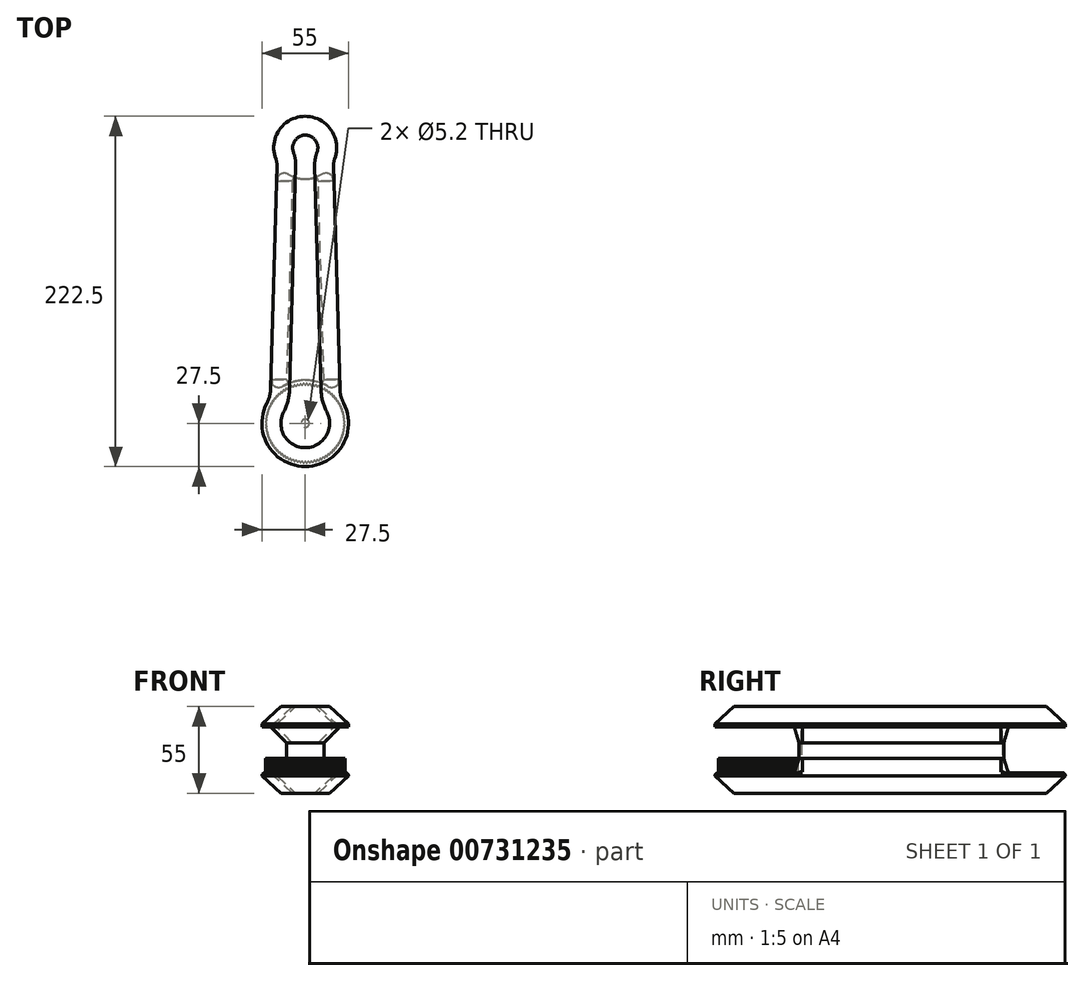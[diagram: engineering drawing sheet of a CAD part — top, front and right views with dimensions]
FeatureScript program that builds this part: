
annotation { "Feature Type Name" : "Feature", "Feature Type Description" : "" }
export const myFeature = defineFeature(function(context is Context, id is Id, definition is map)
    precondition{}
    {
        {
            assignVariable(context, id + "F0", {"name" : "Teeth", "anyValue" : 80});
        }
        {
            var Q0;
            Q0=qCreatedBy(makeId("Top.planeOp"),FACE);
            var sketch = newSketch(context, id + "F1", { "sketchPlane" : qUnion([Q0])});
            skCircle(sketch, "E0", {"center": v(0, 0) * mm, "radius": 25.21 * mm});
            skSolve(sketch);
        }
        {
            var Q0;
            Q0=qCreatedBy(makeId("Top.planeOp"),FACE);
            var sketch = newSketch(context, id + "F2", { "sketchPlane" : qUnion([Q0])});
            skArc(sketch, "E1.0", {"start": v(0.79, 25.2) * mm, "mid": v(0, 25.21) * mm, "end": v(-0.79, 25.2) * mm});
            skLineSegment(sketch, "E2", {"start": v(0, 0) * mm, "end": v(0, 25.03) * mm, "construction": true});
            skArc(sketch, "E3", {"start": v(0, 24.42) * mm, "mid": v(-0.38, 24.56) * mm, "end": v(-0.6, 24.9) * mm});
            skArc(sketch, "E4", {"start": v(-0.6, 24.9) * mm, "mid": v(-0.63, 25) * mm, "end": v(-0.68, 25.1) * mm});
            skArc(sketch, "E5", {"start": v(-0.68, 25.1) * mm, "mid": v(-0.72, 25.16) * mm, "end": v(-0.79, 25.2) * mm});
            skArc(sketch, "E6.MirrorCS", {"start": v(0, 24.42) * mm, "mid": v(0.38, 24.56) * mm, "end": v(0.6, 24.9) * mm});
            skArc(sketch, "E7.MirrorCS", {"start": v(0.68, 25.1) * mm, "mid": v(0.72, 25.16) * mm, "end": v(0.79, 25.2) * mm});
            skArc(sketch, "E8.MirrorCS", {"start": v(0.6, 24.9) * mm, "mid": v(0.63, 25) * mm, "end": v(0.68, 25.1) * mm});
            skSolve(sketch);
        }
        {
            var Q0;
            Q0=qSketchRegion(id+"F1",true);
            extrude(context, id + "F3", {"entities" : qUnion([Q0]), "depth" : 9 * mm, "offsetDistance" : 25 * mm});
        }
        {
            var Q0;
            Q0=makeQuery(id+"F2.imprint","IMPRINT",FACE,{"disambiguationData":[TD([[makeQuery(id+"F2.imprint","IMPRINT",EDGE,{"derivedFrom":sQuery(id+"F2.wireOp",EDGE,"E1.0")}),1.0]])]});
            extrude(context, id + "F4", {"entities" : qUnion([Q0]), "depth" : 25 * mm, "offsetDistance" : 25 * mm});
        }
        {
            var Q0;
            Q0=makeQuery(id+"F4.opExtrude","SWEPT_BODY",BODY,{"disambiguationData":[OSD([sQuery(id+"F2.wireOp",EDGE,"E1.0"),sQuery(id+"F2.wireOp",EDGE,"E3"),sQuery(id+"F2.wireOp",EDGE,"E4"),sQuery(id+"F2.wireOp",EDGE,"E5"),sQuery(id+"F2.wireOp",EDGE,"E6.MirrorCS"),sQuery(id+"F2.wireOp",EDGE,"E7.MirrorCS"),sQuery(id+"F2.wireOp",EDGE,"E8.MirrorCS")])]});
            var Q1;
            Q1=sQuery(id+"F1.wireOp",EDGE,"E0");
            circularPattern(context, id + "F5", {"operationType" : NewBodyOperationType.REMOVE, "entities" : qUnion([Q0]), "axis" : qUnion([Q1]), "angle" : 360 * degree, "instanceCount" : getVariable(context, 'Teeth'), "equalSpace" : true});
        }
        {
            var Q0;
            Q0=qCreatedBy(makeId("Top.planeOp"),FACE);
            var sketch = newSketch(context, id + "F6", { "sketchPlane" : qUnion([Q0])});
            skCircle(sketch, "E9", {"center": v(0, 0) * mm, "radius": 2.6 * mm});
            skSolve(sketch);
        }
        {
            var Q0;
            Q0=qSketchRegion(id+"F6",true);
            var Q1;
            Q1=sQuery(id+"F6.wireOp",EDGE,"E9");
            extrude(context, id + "F7", {"entities" : qUnion([Q0]), "operationType" : NewBodyOperationType.REMOVE, "surfaceEntities" : qUnion([Q1]), "endBound" : BoundingType.THROUGH_ALL, "depth" : 25 * mm, "offsetDistance" : 25 * mm});
        }
        {
            var Q0;
            Q0=makeQuery(id+"F3.opExtrude","SWEPT_BODY",BODY,{"disambiguationData":[OSD([sQuery(id+"F1.wireOp",EDGE,"E0")])]});
            transform(context, id + "F8", {"entities" : qUnion([Q0]), "transformType" : TransformType.TRANSLATION_3D, "dx" : 0 * mm, "dy" : 0 * mm, "dz" : 0 * mm, "makeCopy" : true});
        }
        {
            var Q0;
            Q0=qCreatedBy(makeId("Top.planeOp"),FACE);
            var sketch = newSketch(context, id + "F9", { "sketchPlane" : qUnion([Q0])});
            skArc(sketch, "E10", {"start": v(-24.31, 12.85) * mm, "mid": v(0, -27.5) * mm, "end": v(24.31, 12.85) * mm});
            skLineSegment(sketch, "E11", {"start": v(0, 0) * mm, "end": v(0, 175) * mm, "construction": true});
            skArc(sketch, "E12", {"start": v(18.66, 167.81) * mm, "mid": v(0, 195) * mm, "end": v(-18.66, 167.81) * mm});
            skLineSegment(sketch, "E13", {"start": v(-18, 163.94) * mm, "end": v(-22, 21.64) * mm});
            skArc(sketch, "E14.filletArc", {"start": v(-24.31, 12.85) * mm, "mid": v(-22.65, 17.11) * mm, "end": v(-22, 21.64) * mm});
            skArc(sketch, "E15.filletArc", {"start": v(-18, 163.94) * mm, "mid": v(-18.14, 165.9) * mm, "end": v(-18.66, 167.81) * mm});
            skLineSegment(sketch, "E16.MirrorCS", {"start": v(18, 163.94) * mm, "end": v(22, 21.64) * mm});
            skArc(sketch, "E17.MirrorCS", {"start": v(18, 163.94) * mm, "mid": v(18.14, 165.9) * mm, "end": v(18.66, 167.81) * mm});
            skArc(sketch, "E18.MirrorCS", {"start": v(24.31, 12.85) * mm, "mid": v(22.65, 17.11) * mm, "end": v(22, 21.64) * mm});
            skSolve(sketch);
        }
        {
            var Q0;
            Q0=makeQuery(id+"F9.imprint","IMPRINT",FACE,{"disambiguationData":[TD([[makeQuery(id+"F9.imprint","IMPRINT",EDGE,{"derivedFrom":sQuery(id+"F9.wireOp",EDGE,"E10")}),1.0]])]});
            extrude(context, id + "F10", {"entities" : qUnion([Q0]), "oppositeDirection" : true, "depth" : 2 * mm, "offsetDistance" : 25 * mm});
        }
        {
            var Q0;
            Q0=makeQuery(id+"F10.opExtrude","CAP_FACE",FACE,{"disambiguationData":[OSD([sQuery(id+"F9.wireOp",EDGE,"E10"),sQuery(id+"F9.wireOp",EDGE,"E12"),sQuery(id+"F9.wireOp",EDGE,"E13"),sQuery(id+"F9.wireOp",EDGE,"E14.filletArc"),sQuery(id+"F9.wireOp",EDGE,"E15.filletArc"),sQuery(id+"F9.wireOp",EDGE,"E16.MirrorCS"),sQuery(id+"F9.wireOp",EDGE,"E17.MirrorCS"),sQuery(id+"F9.wireOp",EDGE,"E18.MirrorCS")])],"isStart":true});
            var sketch = newSketch(context, id + "F11", { "sketchPlane" : qUnion([Q0])});
            skArc(sketch, "E19", {"start": v(14.24, 23.53) * mm, "mid": v(0, 27.5) * mm, "end": v(-14.24, 23.53) * mm});
            skArc(sketch, "E20.0.0", {"start": v(18, 163.94) * mm, "mid": v(18.14, 165.9) * mm, "end": v(18.66, 167.81) * mm});
            skArc(sketch, "E20.0.1", {"start": v(18.66, 167.81) * mm, "mid": v(0, 195) * mm, "end": v(-18.66, 167.81) * mm});
            skArc(sketch, "E20.0.2", {"start": v(-18.66, 167.81) * mm, "mid": v(-18.14, 165.9) * mm, "end": v(-18, 163.94) * mm});
            skLineSegment(sketch, "E20.0.3", {"start": v(-18.28, 153.96) * mm, "end": v(-21.82, 27.95) * mm});
            skArc(sketch, "E20.0.5", {"start": v(-24.31, 12.85) * mm, "mid": v(0, -27.5) * mm, "end": v(24.31, 12.85) * mm});
            skLineSegment(sketch, "E20.0.7", {"start": v(21.82, 27.95) * mm, "end": v(18.28, 153.96) * mm});
            skPoint(sketch, "E21.newPointB", {"position": v(-22, 21.64) * mm});
            skArc(sketch, "E21.filletArc", {"start": v(-21.82, 27.95) * mm, "mid": v(-19.34, 23.49) * mm, "end": v(-14.24, 23.53) * mm});
            skPoint(sketch, "E22.newPointB", {"position": v(22, 21.64) * mm});
            skArc(sketch, "E22.filletArc", {"start": v(14.24, 23.53) * mm, "mid": v(19.34, 23.49) * mm, "end": v(21.82, 27.95) * mm});
            skArc(sketch, "E23", {"start": v(-10.63, 158.06) * mm, "mid": v(0, 155) * mm, "end": v(10.63, 158.06) * mm});
            skArc(sketch, "E24.filletArc", {"start": v(-10.63, 158.06) * mm, "mid": v(-15.64, 158.23) * mm, "end": v(-18.28, 153.96) * mm});
            skArc(sketch, "E25.filletArc", {"start": v(18.28, 153.96) * mm, "mid": v(15.64, 158.23) * mm, "end": v(10.63, 158.06) * mm});
            skSolve(sketch);
        }
        {
            var Q0;
            Q0=qCreatedBy(makeId("Top.planeOp"),FACE);
            cPlane(context, id + "F12", {"entities" : qUnion([Q0]), "cplaneType" : CPlaneType.OFFSET, "offset" : 9 * mm, "width" : 150 * mm, "height" : 150 * mm});
        }
        {
            var Q0;
            Q0=qCreatedBy(id+"F12.planeOp",FACE);
            var sketch = newSketch(context, id + "F13", { "sketchPlane" : qUnion([Q0])});
            skArc(sketch, "E26.0", {"start": v(14.24, 23.53) * mm, "mid": v(0, 27.5) * mm, "end": v(-14.24, 23.53) * mm});
            skLineSegment(sketch, "E26.4", {"start": v(-18.28, 153.96) * mm, "end": v(-21.82, 27.95) * mm});
            skLineSegment(sketch, "E26.6", {"start": v(21.82, 27.95) * mm, "end": v(18.28, 153.96) * mm});
            skPoint(sketch, "E26.7", {"position": v(-22, 21.64) * mm});
            skArc(sketch, "E26.8", {"start": v(-21.82, 27.95) * mm, "mid": v(-19.34, 23.49) * mm, "end": v(-14.24, 23.53) * mm});
            skPoint(sketch, "E26.9", {"position": v(22, 21.64) * mm});
            skArc(sketch, "E26.10", {"start": v(14.24, 23.53) * mm, "mid": v(19.34, 23.49) * mm, "end": v(21.82, 27.95) * mm});
            skLineSegment(sketch, "E27.2", {"start": v(11.9, 24.79) * mm, "end": v(8.2, 156.76) * mm});
            skLineSegment(sketch, "E27.3", {"start": v(-8.2, 156.76) * mm, "end": v(-11.9, 24.79) * mm});
            skArc(sketch, "E28", {"start": v(9.16, 25.93) * mm, "mid": v(11, 26.2) * mm, "end": v(11.82, 27.87) * mm});
            skArc(sketch, "E29", {"start": v(-11.82, 27.87) * mm, "mid": v(-11, 26.2) * mm, "end": v(-9.16, 25.93) * mm});
            skArc(sketch, "E30.0", {"start": v(-10.63, 158.06) * mm, "mid": v(0, 155) * mm, "end": v(10.63, 158.06) * mm});
            skArc(sketch, "E31", {"start": v(-5.7, 155.83) * mm, "mid": v(-7.45, 155.53) * mm, "end": v(-8.28, 153.97) * mm});
            skArc(sketch, "E32", {"start": v(8.28, 153.97) * mm, "mid": v(7.45, 155.53) * mm, "end": v(5.7, 155.83) * mm});
            skSolve(sketch);
        }
        {
            var Q1;
            Q1=makeQuery(id+"F11.imprint","IMPRINT",FACE,{"disambiguationData":[TD([[makeQuery(id+"F11.imprint","IMPRINT",EDGE,{"derivedFrom":sQuery(id+"F11.wireOp",EDGE,"E19")}),-1.0]])]});
            var Q2;
            {var subQ3=sQuery(id+"F13.wireOp",EDGE,"E28");Q2=makeQuery(id+"F13.imprint","IMPRINT",FACE,{"disambiguationData":[TD([[makeQuery(id+"F13.imprint","IMPRINT",EDGE,{"derivedFrom":subQ3}),1.0]])]});}
            loft(context, id + "F14", {"operationType" : NewBodyOperationType.ADD, "sheetProfilesArray" : [{ "sheetProfileEntities" : qUnion([Q1]) }, { "sheetProfileEntities" : qUnion([Q2]) }]});
        }
        {
            var Q0;
            Q0=qCreatedBy(makeId("Top.planeOp"),FACE);
            cPlane(context, id + "F15", {"entities" : qUnion([Q0]), "cplaneType" : CPlaneType.OFFSET, "offset" : 13 * mm, "oppositeDirection" : true, "width" : 150 * mm, "height" : 150 * mm});
        }
        {
            var Q0;
            Q0=qCreatedBy(id+"F15.planeOp",FACE);
            var sketch = newSketch(context, id + "F16", { "sketchPlane" : qUnion([Q0])});
            skArc(sketch, "E33.0.0", {"start": v(18.66, 167.81) * mm, "mid": v(18.14, 165.9) * mm, "end": v(18, 163.94) * mm});
            skLineSegment(sketch, "E33.0.1", {"start": v(18, 163.94) * mm, "end": v(22, 21.64) * mm});
            skArc(sketch, "E33.0.2", {"start": v(22, 21.64) * mm, "mid": v(22.65, 17.11) * mm, "end": v(24.31, 12.85) * mm});
            skArc(sketch, "E33.0.3", {"start": v(24.31, 12.85) * mm, "mid": v(0, -27.5) * mm, "end": v(-24.31, 12.85) * mm});
            skArc(sketch, "E33.0.4", {"start": v(-24.31, 12.85) * mm, "mid": v(-22.65, 17.11) * mm, "end": v(-22, 21.64) * mm});
            skLineSegment(sketch, "E33.0.5", {"start": v(-22, 21.64) * mm, "end": v(-18, 163.94) * mm});
            skArc(sketch, "E33.0.6", {"start": v(-18, 163.94) * mm, "mid": v(-18.14, 165.9) * mm, "end": v(-18.66, 167.81) * mm});
            skArc(sketch, "E33.0.7", {"start": v(-18.66, 167.81) * mm, "mid": v(0, 195) * mm, "end": v(18.66, 167.81) * mm});
            skArc(sketch, "E34.0", {"start": v(-13.7, 7.24) * mm, "mid": v(-11.04, 14.06) * mm, "end": v(-10, 21.3) * mm});
            skArc(sketch, "E34.1", {"start": v(13.7, 7.24) * mm, "mid": v(0, -15.5) * mm, "end": v(-13.7, 7.24) * mm});
            skLineSegment(sketch, "E34.2", {"start": v(-10, 21.3) * mm, "end": v(-6, 163.6) * mm});
            skArc(sketch, "E34.3", {"start": v(10, 21.3) * mm, "mid": v(11.04, 14.06) * mm, "end": v(13.7, 7.24) * mm});
            skArc(sketch, "E34.4", {"start": v(-6, 163.6) * mm, "mid": v(-6.31, 167.94) * mm, "end": v(-7.47, 172.13) * mm});
            skArc(sketch, "E34.5", {"start": v(-7.47, 172.13) * mm, "mid": v(0, 183) * mm, "end": v(7.47, 172.13) * mm});
            skArc(sketch, "E34.6", {"start": v(7.47, 172.13) * mm, "mid": v(6.31, 167.94) * mm, "end": v(6, 163.6) * mm});
            skLineSegment(sketch, "E34.7", {"start": v(6, 163.6) * mm, "end": v(10, 21.3) * mm});
            skSolve(sketch);
        }
        {
            var Q1;
            Q1=makeQuery(id+"F10.opExtrude","CAP_FACE",FACE,{"disambiguationData":[OSD([sQuery(id+"F9.wireOp",EDGE,"E10"),sQuery(id+"F9.wireOp",EDGE,"E12"),sQuery(id+"F9.wireOp",EDGE,"E13"),sQuery(id+"F9.wireOp",EDGE,"E14.filletArc"),sQuery(id+"F9.wireOp",EDGE,"E15.filletArc"),sQuery(id+"F9.wireOp",EDGE,"E16.MirrorCS"),sQuery(id+"F9.wireOp",EDGE,"E17.MirrorCS"),sQuery(id+"F9.wireOp",EDGE,"E18.MirrorCS")])],"isStart":false});
            var Q2;
            Q2=makeQuery(id+"F16.imprint","IMPRINT",FACE,{"disambiguationData":[TD([[makeQuery(id+"F16.imprint","IMPRINT",EDGE,{"derivedFrom":sQuery(id+"F16.wireOp",EDGE,"E34.0")}),-1.0]])]});
            loft(context, id + "F17", {"operationType" : NewBodyOperationType.ADD, "sheetProfilesArray" : [{ "sheetProfileEntities" : qUnion([Q1]) }, { "sheetProfileEntities" : qUnion([Q2]) }]});
        }
        {
            var Q0;
            {var subQ3=sQuery(id+"F13.wireOp",EDGE,"E28");Q0=makeQuery(id+"F14.opLoft","CAP_FACE",FACE,{"disambiguationData":[OSD([makeQuery(id+"F13.imprint","IMPRINT",FACE,{"disambiguationData":[TD([[makeQuery(id+"F13.imprint","IMPRINT",EDGE,{"derivedFrom":subQ3}),1.0]])]})])],"isStart":true});}
            extrude(context, id + "F18", {"entities" : qUnion([Q0]), "operationType" : NewBodyOperationType.ADD, "depth" : 10 * mm, "offsetDistance" : 25 * mm});
        }
        {
            var Q0;
            Q0=makeQuery(id+"F10.opExtrude","CAP_EDGE",EDGE,{"disambiguationData":[OSD([sQuery(id+"F9.wireOp",EDGE,"E12")])],"isStart":true});
            fillet(context, id + "F19", {"entities" : qUnion([Q0]), "radius" : 2 * mm, "tangentPropagation" : true, "allowEdgeOverflow" : false});
        }
        {
            var Q0;
            Q0=qCreatedBy(id+"F12.planeOp",FACE);
            cPlane(context, id + "F20", {"entities" : qUnion([Q0]), "cplaneType" : CPlaneType.OFFSET, "offset" : 20 * mm, "width" : 150 * mm, "height" : 150 * mm});
        }
        {
            var Q0;
            Q0=qCreatedBy(id+"F20.planeOp",FACE);
            var sketch = newSketch(context, id + "F21", { "sketchPlane" : qUnion([Q0])});
            skArc(sketch, "E35.0", {"start": v(14.24, 23.53) * mm, "mid": v(0, 27.5) * mm, "end": v(-14.24, 23.53) * mm});
            skLineSegment(sketch, "E35.4", {"start": v(-18.28, 153.96) * mm, "end": v(-21.82, 27.95) * mm});
            skLineSegment(sketch, "E35.6", {"start": v(21.82, 27.95) * mm, "end": v(18.28, 153.96) * mm});
            skPoint(sketch, "E35.7", {"position": v(-22, 21.64) * mm});
            skArc(sketch, "E35.8", {"start": v(-21.82, 27.95) * mm, "mid": v(-19.34, 23.49) * mm, "end": v(-14.24, 23.53) * mm});
            skPoint(sketch, "E35.9", {"position": v(22, 21.64) * mm});
            skArc(sketch, "E35.10", {"start": v(14.24, 23.53) * mm, "mid": v(19.34, 23.49) * mm, "end": v(21.82, 27.95) * mm});
            skArc(sketch, "E35.11", {"start": v(-10.63, 158.06) * mm, "mid": v(0, 155) * mm, "end": v(10.63, 158.06) * mm});
            skArc(sketch, "E35.12", {"start": v(-10.63, 158.06) * mm, "mid": v(-15.64, 158.23) * mm, "end": v(-18.28, 153.96) * mm});
            skArc(sketch, "E35.13", {"start": v(18.28, 153.96) * mm, "mid": v(15.64, 158.23) * mm, "end": v(10.63, 158.06) * mm});
            skSolve(sketch);
        }
        {
            var Q1;
            {var subQ3=sQuery(id+"F13.wireOp",EDGE,"E28");Q1=makeQuery(id+"F18.opExtrude","CAP_FACE",FACE,{"disambiguationData":[OSD([makeQuery(id+"F13.imprint","IMPRINT",FACE,{"disambiguationData":[TD([[makeQuery(id+"F13.imprint","IMPRINT",EDGE,{"derivedFrom":subQ3}),1.0]])]})])],"isStart":false});}
            var Q2;
            Q2=makeQuery(id+"F21.imprint","IMPRINT",FACE,{"disambiguationData":[TD([[makeQuery(id+"F21.imprint","IMPRINT",EDGE,{"derivedFrom":sQuery(id+"F21.wireOp",EDGE,"E35.0")}),-1.0]])]});
            loft(context, id + "F22", {"sheetProfilesArray" : [{ "sheetProfileEntities" : qUnion([Q1]) }, { "sheetProfileEntities" : qUnion([Q2]) }]});
        }
        {
            var Q0;
            Q0=qCreatedBy(id+"F20.planeOp",FACE);
            var sketch = newSketch(context, id + "F23", { "sketchPlane" : qUnion([Q0])});
            skArc(sketch, "E36.0", {"start": v(-24.31, 12.85) * mm, "mid": v(0, -27.5) * mm, "end": v(24.31, 12.85) * mm});
            skLineSegment(sketch, "E36.1", {"start": v(0, 0) * mm, "end": v(0, 175) * mm});
            skArc(sketch, "E36.2", {"start": v(18.66, 167.81) * mm, "mid": v(0, 195) * mm, "end": v(-18.66, 167.81) * mm});
            skLineSegment(sketch, "E36.3", {"start": v(-18, 163.94) * mm, "end": v(-22, 21.64) * mm});
            skArc(sketch, "E36.4", {"start": v(-24.31, 12.85) * mm, "mid": v(-22.65, 17.11) * mm, "end": v(-22, 21.64) * mm});
            skArc(sketch, "E36.5", {"start": v(-18, 163.94) * mm, "mid": v(-18.14, 165.9) * mm, "end": v(-18.66, 167.81) * mm});
            skLineSegment(sketch, "E36.6", {"start": v(18, 163.94) * mm, "end": v(22, 21.64) * mm});
            skArc(sketch, "E36.7", {"start": v(18, 163.94) * mm, "mid": v(18.14, 165.9) * mm, "end": v(18.66, 167.81) * mm});
            skArc(sketch, "E36.8", {"start": v(24.31, 12.85) * mm, "mid": v(22.65, 17.11) * mm, "end": v(22, 21.64) * mm});
            skSolve(sketch);
        }
        {
            var Q0;
            Q0=makeQuery(id+"F23.imprint","IMPRINT",FACE,{"disambiguationData":[TD([[makeQuery(id+"F23.imprint","IMPRINT",EDGE,{"derivedFrom":sQuery(id+"F23.wireOp",EDGE,"E36.0")}),1.0]])]});
            extrude(context, id + "F24", {"entities" : qUnion([Q0]), "operationType" : NewBodyOperationType.ADD, "depth" : 2 * mm, "offsetDistance" : 25 * mm});
        }
        {
            var Q0;
            Q0=qCreatedBy(id+"F20.planeOp",FACE);
            cPlane(context, id + "F25", {"entities" : qUnion([Q0]), "cplaneType" : CPlaneType.OFFSET, "offset" : 13 * mm, "width" : 150 * mm, "height" : 150 * mm});
        }
        {
            var Q0;
            Q0=qCreatedBy(id+"F25.planeOp",FACE);
            var sketch = newSketch(context, id + "F26", { "sketchPlane" : qUnion([Q0])});
            skArc(sketch, "E37.0", {"start": v(18.66, 167.81) * mm, "mid": v(18.14, 165.9) * mm, "end": v(18, 163.94) * mm});
            skLineSegment(sketch, "E37.1", {"start": v(18, 163.94) * mm, "end": v(22, 21.64) * mm});
            skArc(sketch, "E37.2", {"start": v(22, 21.64) * mm, "mid": v(22.65, 17.11) * mm, "end": v(24.31, 12.85) * mm});
            skArc(sketch, "E37.3", {"start": v(24.31, 12.85) * mm, "mid": v(0, -27.5) * mm, "end": v(-24.31, 12.85) * mm});
            skArc(sketch, "E37.4", {"start": v(-24.31, 12.85) * mm, "mid": v(-22.65, 17.11) * mm, "end": v(-22, 21.64) * mm});
            skLineSegment(sketch, "E37.5", {"start": v(-22, 21.64) * mm, "end": v(-18, 163.94) * mm});
            skArc(sketch, "E37.6", {"start": v(-18, 163.94) * mm, "mid": v(-18.14, 165.9) * mm, "end": v(-18.66, 167.81) * mm});
            skArc(sketch, "E37.7", {"start": v(-18.66, 167.81) * mm, "mid": v(0, 195) * mm, "end": v(18.66, 167.81) * mm});
            skArc(sketch, "E37.8", {"start": v(-13.7, 7.24) * mm, "mid": v(-11.04, 14.06) * mm, "end": v(-10, 21.3) * mm});
            skArc(sketch, "E37.9", {"start": v(13.7, 7.24) * mm, "mid": v(0, -15.5) * mm, "end": v(-13.7, 7.24) * mm});
            skLineSegment(sketch, "E37.10", {"start": v(-10, 21.3) * mm, "end": v(-6, 163.6) * mm});
            skArc(sketch, "E37.11", {"start": v(10, 21.3) * mm, "mid": v(11.04, 14.06) * mm, "end": v(13.7, 7.24) * mm});
            skArc(sketch, "E37.12", {"start": v(-6, 163.6) * mm, "mid": v(-6.31, 167.94) * mm, "end": v(-7.47, 172.13) * mm});
            skArc(sketch, "E37.13", {"start": v(-7.47, 172.13) * mm, "mid": v(0, 183) * mm, "end": v(7.47, 172.13) * mm});
            skArc(sketch, "E37.14", {"start": v(7.47, 172.13) * mm, "mid": v(6.31, 167.94) * mm, "end": v(6, 163.6) * mm});
            skLineSegment(sketch, "E37.15", {"start": v(6, 163.6) * mm, "end": v(10, 21.3) * mm});
            skSolve(sketch);
        }
        {
            var Q1;
            Q1=makeQuery(id+"F24.opExtrude","CAP_FACE",FACE,{"disambiguationData":[OSD([sQuery(id+"F23.wireOp",EDGE,"E36.0"),sQuery(id+"F23.wireOp",EDGE,"E36.2"),sQuery(id+"F23.wireOp",EDGE,"E36.3"),sQuery(id+"F23.wireOp",EDGE,"E36.4"),sQuery(id+"F23.wireOp",EDGE,"E36.5"),sQuery(id+"F23.wireOp",EDGE,"E36.6"),sQuery(id+"F23.wireOp",EDGE,"E36.7"),sQuery(id+"F23.wireOp",EDGE,"E36.8")])],"isStart":false});
            var Q2;
            Q2=makeQuery(id+"F26.imprint","IMPRINT",FACE,{"disambiguationData":[TD([[makeQuery(id+"F26.imprint","IMPRINT",EDGE,{"derivedFrom":sQuery(id+"F26.wireOp",EDGE,"E37.8")}),-1.0]])]});
            loft(context, id + "F27", {"operationType" : NewBodyOperationType.ADD, "sheetProfilesArray" : [{ "sheetProfileEntities" : qUnion([Q1]) }, { "sheetProfileEntities" : qUnion([Q2]) }]});
        }
    });
